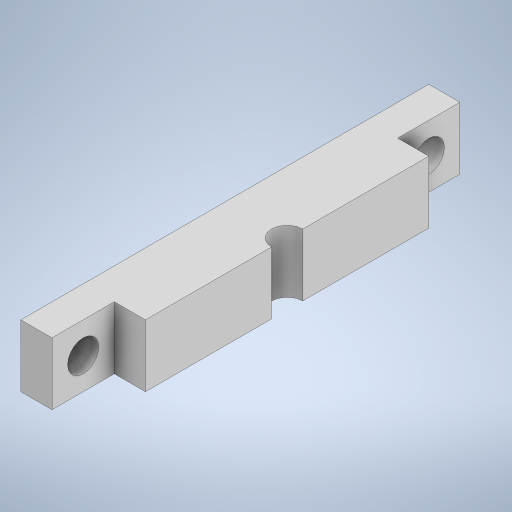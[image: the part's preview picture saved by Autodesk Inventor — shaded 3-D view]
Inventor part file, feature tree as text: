
AUTODESK INVENTOR PART (.ipt)
format: ipt  version: 2023 (Build 270158000, 158)  size: 262,656 bytes
history: native  units: mm
features: extrude x3, sketch x2
ambient origin geometry x8: Origin, YZ Plane, XZ Plane, XY Plane, X Axis, Y Axis, Z Axis, Center Point
bodies: Solid1 (feature_tree)
feature tree (5):
  sketch  "Sketch1"  dims[d0=10.0mm d1=0.0mm d2=5.0mm d3=0.0mm]
  extrude  "Extrusion1"  Depth=5.0mm TaperAngle=0.0deg
  extrude  "Extrusion2"  Depth=10.0mm TaperAngle=0.0deg
  extrude  "Extrusion4"  [1 undecoded]
  sketch  "Sketch4"  dims[d7=5.0mm d8=10.0mm d9=0.0mm]
note: 1 required parameter value undecoded (feature->parameter linkage not recoverable at this tier; creation-order binding heuristic only, values carry confidence <= 0.55)
